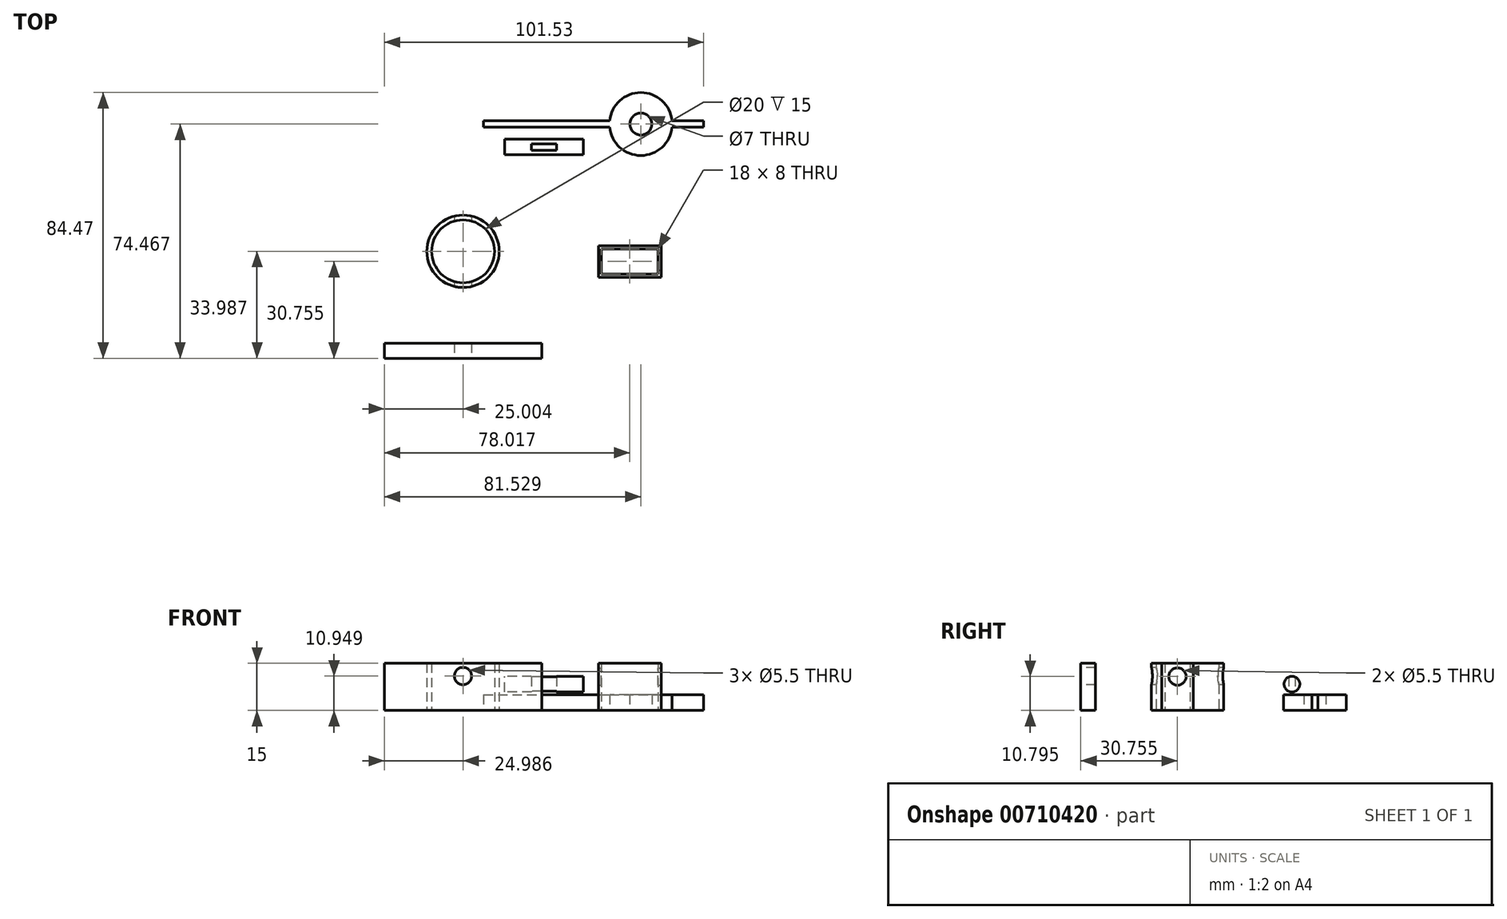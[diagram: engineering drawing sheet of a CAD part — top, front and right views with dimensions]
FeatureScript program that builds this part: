
annotation { "Feature Type Name" : "Feature", "Feature Type Description" : "" }
export const myFeature = defineFeature(function(context is Context, id is Id, definition is map)
    precondition{}
    {
        {
            var Q0;
            Q0=qCreatedBy(makeId("Top.planeOp"),FACE);
            var sketch = newSketch(context, id + "F0", { "sketchPlane" : qUnion([Q0])});
            skCircle(sketch, "E0", {"center": v(43.26, -23.75) * mm, "radius": 10 * mm});
            skLineSegment(sketch, "E1.bottom", {"start": v(-6.74, -22.75) * mm, "end": v(63.26, -22.75) * mm});
            skLineSegment(sketch, "E1.top", {"start": v(-6.74, -24.75) * mm, "end": v(63.26, -24.75) * mm});
            skLineSegment(sketch, "E1.left", {"start": v(-6.74, -22.75) * mm, "end": v(-6.74, -24.75) * mm});
            skLineSegment(sketch, "E1.right", {"start": v(63.26, -22.75) * mm, "end": v(63.26, -24.75) * mm});
            skCircle(sketch, "E2", {"center": v(43.26, -23.75) * mm, "radius": 3.5 * mm});
            skPoint(sketch, "E3.centerSnap0", {"position": v(63.26, -23.75) * mm});
            skSolve(sketch);
        }
        {
            var Q0;
            {var subQ0=sQuery(id+"F0.wireOp",EDGE,"E1.bottom");var subQ1=sQuery(id+"F0.wireOp",EDGE,"E0");var subQ2=makeQuery(id+"F0.imprint","INTERSECT",VERTEX,{"disambiguationData":[OD(0.0)],"derivedFrom":[subQ1,subQ0]});Q0=makeQuery(id+"F0.imprint","IMPRINT",FACE,{"disambiguationData":[TD([[makeQuery(id+"F0.imprint","IMPRINT",EDGE,{"disambiguationData":[TD([[subQ2,1.0]])],"derivedFrom":subQ1}),1.0]])]});}
            var Q1;
            {var subQ0=sQuery(id+"F0.wireOp",EDGE,"E1.top");var subQ1=sQuery(id+"F0.wireOp",EDGE,"E0");var subQ2=makeQuery(id+"F0.imprint","INTERSECT",VERTEX,{"disambiguationData":[OD(0.0)],"derivedFrom":[subQ1,subQ0]});Q1=makeQuery(id+"F0.imprint","IMPRINT",FACE,{"disambiguationData":[TD([[makeQuery(id+"F0.imprint","IMPRINT",EDGE,{"disambiguationData":[TD([[subQ2,-1.0]])],"derivedFrom":subQ1}),1.0]])]});}
            var Q2;
            {var subQ0=sQuery(id+"F0.wireOp",EDGE,"E1.bottom");var subQ1=sQuery(id+"F0.wireOp",EDGE,"E0");var subQ2=makeQuery(id+"F0.imprint","INTERSECT",VERTEX,{"disambiguationData":[OD(0.0)],"derivedFrom":[subQ1,subQ0]});Q2=makeQuery(id+"F0.imprint","IMPRINT",FACE,{"disambiguationData":[TD([[makeQuery(id+"F0.imprint","IMPRINT",EDGE,{"disambiguationData":[TD([[subQ2,-1.0]])],"derivedFrom":subQ1}),1.0]])]});}
            var Q3;
            {var subQ0=sQuery(id+"F0.wireOp",EDGE,"E1.bottom");var subQ1=sQuery(id+"F0.wireOp",EDGE,"E0");var subQ2=makeQuery(id+"F0.imprint","INTERSECT",VERTEX,{"disambiguationData":[OD(1.0)],"derivedFrom":[subQ1,subQ0]});Q3=makeQuery(id+"F0.imprint","IMPRINT",FACE,{"disambiguationData":[TD([[makeQuery(id+"F0.imprint","IMPRINT",EDGE,{"disambiguationData":[TD([[subQ2,1.0]])],"derivedFrom":subQ1}),1.0]])]});}
            var Q4;
            {var subQ5=sQuery(id+"F0.wireOp",EDGE,"E1.left");Q4=makeQuery(id+"F0.imprint","IMPRINT",FACE,{"disambiguationData":[TD([[makeQuery(id+"F0.imprint","IMPRINT",EDGE,{"derivedFrom":subQ5}),1.0]])]});}
            var Q5;
            {var subQ5=sQuery(id+"F0.wireOp",EDGE,"E1.right");Q5=makeQuery(id+"F0.imprint","IMPRINT",FACE,{"disambiguationData":[TD([[makeQuery(id+"F0.imprint","IMPRINT",EDGE,{"derivedFrom":subQ5}),-1.0]])]});}
            var Q6;
            {var subQ0=sQuery(id+"F0.wireOp",EDGE,"E1.bottom");var subQ1=sQuery(id+"F0.wireOp",EDGE,"E0");var subQ2=makeQuery(id+"F0.imprint","INTERSECT",VERTEX,{"disambiguationData":[OD(1.0)],"derivedFrom":[subQ1,subQ0]});Q6=makeQuery(id+"F0.imprint","IMPRINT",FACE,{"disambiguationData":[TD([[makeQuery(id+"F0.imprint","IMPRINT",EDGE,{"disambiguationData":[TD([[subQ2,1.0]])],"derivedFrom":subQ1}),-1.0]])]});}
            var Q7;
            {var subQ3=sQuery(id+"F0.wireOp",EDGE,"SQabRNZO-buC3-TYtJ-Hyej-rsNntmHWiWTi");Q7=makeQuery(id+"F0.imprint","IMPRINT",FACE,{"disambiguationData":[TD([[makeQuery(id+"F0.imprint","IMPRINT",EDGE,{"derivedFrom":subQ3}),-1.0]])]});}
            extrude(context, id + "F1", {"entities" : qUnion([Q0, Q1, Q2, Q3, Q4, Q5, Q6, Q7]), "depth" : 5 * mm, "offsetDistance" : 25 * mm});
        }
        {
            var Q0;
            Q0=qCreatedBy(makeId("Top.planeOp"),FACE);
            var sketch = newSketch(context, id + "F2", { "sketchPlane" : qUnion([Q0])});
            skCircle(sketch, "E4", {"center": v(-13.27, -64.23) * mm, "radius": 11.5 * mm});
            skCircle(sketch, "E5", {"center": v(-13.27, -64.23) * mm, "radius": 10 * mm});
            skLineSegment(sketch, "E6.bottom", {"start": v(-38.27, -93.5) * mm, "end": v(11.73, -93.5) * mm});
            skLineSegment(sketch, "E6.top", {"start": v(-38.27, -98.22) * mm, "end": v(11.73, -98.22) * mm});
            skLineSegment(sketch, "E6.left", {"start": v(-38.27, -93.5) * mm, "end": v(-38.27, -98.22) * mm});
            skLineSegment(sketch, "E6.right", {"start": v(11.73, -93.5) * mm, "end": v(11.73, -98.22) * mm});
            skSolve(sketch);
        }
        {
            var Q0;
            Q0=makeQuery(id+"F2.imprint","IMPRINT",FACE,{"disambiguationData":[TD([[makeQuery(id+"F2.imprint","IMPRINT",EDGE,{"derivedFrom":sQuery(id+"F2.wireOp",EDGE,"E4")}),1.0]])]});
            var Q1;
            Q1=makeQuery(id+"F2.imprint","IMPRINT",FACE,{"disambiguationData":[TD([[makeQuery(id+"F2.imprint","IMPRINT",EDGE,{"derivedFrom":sQuery(id+"F2.wireOp",EDGE,"E6.bottom")}),-1.0]])]});
            extrude(context, id + "F3", {"entities" : qUnion([Q0, Q1]), "depth" : 15 * mm, "offsetDistance" : 25 * mm});
        }
        {
            var Q0;
            Q0=makeQuery(id+"F3.opExtrude","SWEPT_FACE",FACE,{"disambiguationData":[OSD([sQuery(id+"F2.wireOp",EDGE,"E6.top")])]});
            var sketch = newSketch(context, id + "F4", { "sketchPlane" : qUnion([Q0])});
            skCircle(sketch, "E7", {"center": v(-13.28, 10.95) * mm, "radius": 3.5 * mm});
            skSolve(sketch);
        }
        {
            var Q0;
            Q0=sQuery(id+"F4.wireOp",VERTEX,"E7.center");
            var Q1;
            Q1=makeQuery(id+"F3.opExtrude","SWEPT_BODY",BODY,{"disambiguationData":[OSD([sQuery(id+"F2.wireOp",EDGE,"E4"),sQuery(id+"F2.wireOp",EDGE,"E5")])]});
            var Q2;
            Q2=makeQuery(id+"F3.opExtrude","SWEPT_BODY",BODY,{"disambiguationData":[OSD([sQuery(id+"F2.wireOp",EDGE,"E6.bottom"),sQuery(id+"F2.wireOp",EDGE,"E6.top"),sQuery(id+"F2.wireOp",EDGE,"E6.left"),sQuery(id+"F2.wireOp",EDGE,"E6.right")])]});
            hole(context, id + "F5", {"style" : HoleStyle.SIMPLE, "endStyle" : HoleEndStyle.THROUGH, "standardTappedOrClearance" : lookupTablePath({ "standard" : "ISO", "fit" : "Normal", "size" : "M5", "type" : "Clearance" }), "standardBlindInLast" : lookupTablePath({ "fit" : "Standard", "standard" : "ISO", "size" : "M5", "type" : "Clearance" }), "holeDiameter" : 5.5 * mm, "majorDiameter" : 5 * mm, "isTappedThrough" : true, "tappedDepth" : 12 * mm, "tapClearance" : 3, "locations" : qUnion([Q0]), "scope" : qUnion([Q1, Q2])});
        }
        {
            var Q0;
            Q0=qCreatedBy(makeId("Top.planeOp"),FACE);
            var sketch = newSketch(context, id + "F6", { "sketchPlane" : qUnion([Q0])});
            skLineSegment(sketch, "E8.bottom", {"start": v(29.75, -62.47) * mm, "end": v(49.75, -62.47) * mm});
            skLineSegment(sketch, "E8.top", {"start": v(29.75, -72.47) * mm, "end": v(49.75, -72.47) * mm});
            skLineSegment(sketch, "E8.left", {"start": v(29.75, -62.47) * mm, "end": v(29.75, -72.47) * mm});
            skLineSegment(sketch, "E8.right", {"start": v(49.75, -62.47) * mm, "end": v(49.75, -72.47) * mm});
            skLineSegment(sketch, "E9.bottom", {"start": v(30.75, -63.47) * mm, "end": v(48.75, -63.47) * mm});
            skLineSegment(sketch, "E9.top", {"start": v(30.75, -71.47) * mm, "end": v(48.75, -71.47) * mm});
            skLineSegment(sketch, "E9.left", {"start": v(30.75, -63.47) * mm, "end": v(30.75, -71.47) * mm});
            skLineSegment(sketch, "E9.right", {"start": v(48.75, -63.47) * mm, "end": v(48.75, -71.47) * mm});
            skSolve(sketch);
        }
        {
            var Q0;
            Q0=makeQuery(id+"F6.imprint","IMPRINT",FACE,{"disambiguationData":[TD([[makeQuery(id+"F6.imprint","IMPRINT",EDGE,{"derivedFrom":sQuery(id+"F6.wireOp",EDGE,"E8.bottom")}),-1.0]])]});
            extrude(context, id + "F7", {"entities" : qUnion([Q0]), "depth" : 15 * mm, "offsetDistance" : 25 * mm});
        }
        {
            var Q0;
            Q0=makeQuery(id+"F7.opExtrude","SWEPT_FACE",FACE,{"disambiguationData":[OSD([sQuery(id+"F6.wireOp",EDGE,"E8.right")])]});
            var sketch = newSketch(context, id + "F8", { "sketchPlane" : qUnion([Q0])});
            skCircle(sketch, "E10", {"center": v(-67.47, 10.8) * mm, "radius": 2.75 * mm});
            skSolve(sketch);
        }
        {
            var Q0;
            Q0=makeQuery(id+"F8.imprint","IMPRINT",FACE,{"disambiguationData":[TD([[makeQuery(id+"F8.imprint","IMPRINT",EDGE,{"derivedFrom":sQuery(id+"F8.wireOp",EDGE,"E10")}),1.0]])]});
            extrude(context, id + "F9", {"entities" : qUnion([Q0]), "operationType" : NewBodyOperationType.REMOVE, "oppositeDirection" : true, "depth" : 25 * mm, "offsetDistance" : 25 * mm});
        }
        {
            var Q0;
            Q0=qCreatedBy(makeId("Right.planeOp"),FACE);
            var sketch = newSketch(context, id + "F10", { "sketchPlane" : qUnion([Q0])});
            skCircle(sketch, "E11", {"center": v(-31.05, 8.38) * mm, "radius": 2.5 * mm});
            skSolve(sketch);
        }
        {
            var Q0;
            Q0=makeQuery(id+"F10.imprint","IMPRINT",FACE,{"disambiguationData":[TD([[makeQuery(id+"F10.imprint","IMPRINT",EDGE,{"derivedFrom":sQuery(id+"F10.wireOp",EDGE,"E11")}),1.0]])]});
            extrude(context, id + "F11", {"entities" : qUnion([Q0]), "depth" : 25 * mm, "offsetDistance" : 25 * mm});
        }
        {
            var Q0;
            Q0=qCreatedBy(makeId("Top.planeOp"),FACE);
            var sketch = newSketch(context, id + "F12", { "sketchPlane" : qUnion([Q0])});
            skLineSegment(sketch, "E12.bottom", {"start": v(7.5, -28.56) * mm, "end": v(17.5, -28.56) * mm});
            skLineSegment(sketch, "E12.top", {"start": v(7.5, -33.56) * mm, "end": v(17.5, -33.56) * mm});
            skLineSegment(sketch, "E12.left", {"start": v(7.5, -28.56) * mm, "end": v(7.5, -33.56) * mm});
            skLineSegment(sketch, "E12.right", {"start": v(17.5, -28.56) * mm, "end": v(17.5, -33.56) * mm});
            skLineSegment(sketch, "E13.bottom", {"start": v(8.5, -30.06) * mm, "end": v(16.5, -30.06) * mm});
            skLineSegment(sketch, "E13.top", {"start": v(8.5, -32.06) * mm, "end": v(16.5, -32.06) * mm});
            skLineSegment(sketch, "E13.left", {"start": v(8.5, -30.06) * mm, "end": v(8.5, -32.06) * mm});
            skLineSegment(sketch, "E13.right", {"start": v(16.5, -30.06) * mm, "end": v(16.5, -32.06) * mm});
            skSolve(sketch);
        }
        {
            var Q0;
            Q0=makeQuery(id+"F12.imprint","IMPRINT",FACE,{"disambiguationData":[TD([[makeQuery(id+"F12.imprint","IMPRINT",EDGE,{"derivedFrom":sQuery(id+"F12.wireOp",EDGE,"E13.bottom")}),-1.0]])]});
            extrude(context, id + "F13", {"entities" : qUnion([Q0]), "operationType" : NewBodyOperationType.REMOVE, "depth" : 25 * mm, "offsetDistance" : 25 * mm});
        }
    });
